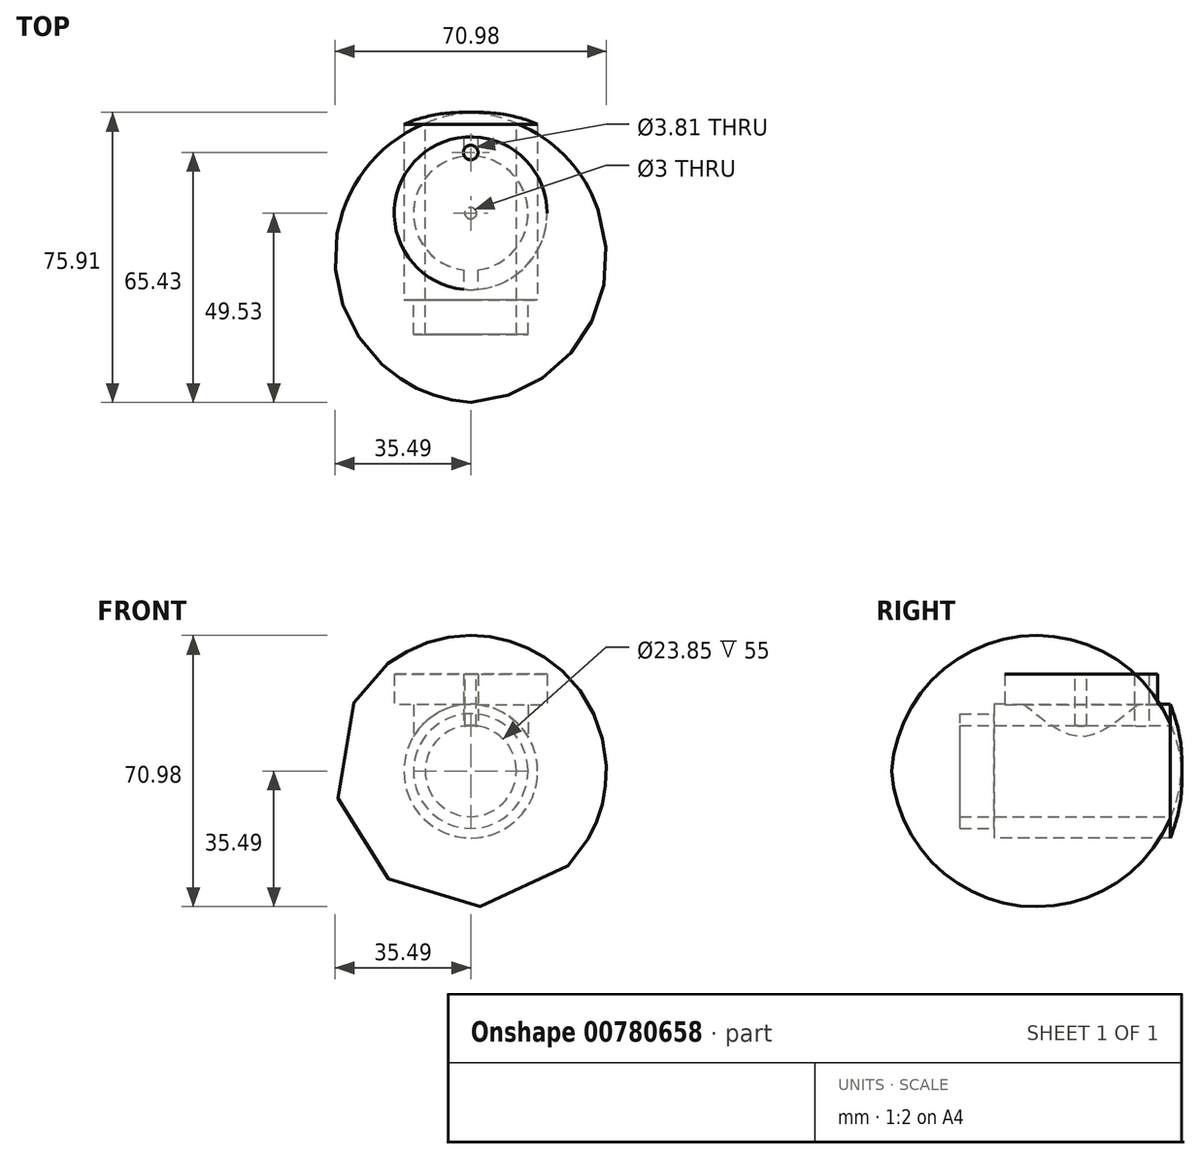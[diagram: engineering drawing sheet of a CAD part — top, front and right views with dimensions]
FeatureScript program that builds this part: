
annotation { "Feature Type Name" : "Feature", "Feature Type Description" : "" }
export const myFeature = defineFeature(function(context is Context, id is Id, definition is map)
    precondition{}
    {
        {
            var Q0;
            Q0=qCreatedBy(makeId("Front.planeOp"),FACE);
            var sketch = newSketch(context, id + "F0", { "sketchPlane" : qUnion([Q0])});
            skCircle(sketch, "E0", {"center": v(0, 0) * mm, "radius": 11.93 * mm});
            skCircle(sketch, "E1", {"center": v(0, 0) * mm, "radius": 15 * mm});
            skSolve(sketch);
        }
        {
            var Q0;
            Q0 = qSketchRegion(id + "F0", true);
            extrude(context, id + "F1", {"entities" : qUnion([Q0]), "depth" : 9 * mm, "offsetDistance" : 25 * mm});
        }
        {
            var Q0;
            Q0=makeQuery(id+"F1.opExtrude","CAP_FACE",FACE,{"disambiguationData":[OSD([sQuery(id+"F0.wireOp",EDGE,"E0"),sQuery(id+"F0.wireOp",EDGE,"E1")])],"isStart":true});
            var sketch = newSketch(context, id + "F2", { "sketchPlane" : qUnion([Q0])});
            skCircle(sketch, "E2", {"center": v(0, 0) * mm, "radius": 11.93 * mm});
            skCircle(sketch, "E3", {"center": v(0, 0) * mm, "radius": 17.5 * mm});
            skSolve(sketch);
        }
        {
            var Q0;
            Q0 = qSketchRegion(id + "F2", true);
            extrude(context, id + "F3", {"entities" : qUnion([Q0]), "operationType" : NewBodyOperationType.ADD, "depth" : 46 * mm, "offsetDistance" : 25 * mm});
        }
        {
            var Q0;
            Q0=qCreatedBy(makeId("Top.planeOp"),FACE);
            var sketch = newSketch(context, id + "F4", { "sketchPlane" : qUnion([Q0])});
            skLineSegment(sketch, "E4", {"start": v(0, 0) * mm, "end": v(0, 46) * mm});
            skLineSegment(sketch, "E5", {"start": v(0, 46) * mm, "end": v(0, 49) * mm});
            skLineSegment(sketch, "E6", {"start": v(0, 46) * mm, "end": v(-17.5, 46) * mm});
            skArc(sketch, "E7", {"start": v(0, 49) * mm, "mid": v(-8.93, 48.54) * mm, "end": v(-17.5, 46) * mm});
            skSolve(sketch);
        }
        {
            var Q0;
            Q0 = qSketchRegion(id + "F4", true);
            var Q1;
            Q1=sQuery(id+"F4.wireOp",EDGE,"E5");
            revolve(context, id + "F5", {"operationType" : NewBodyOperationType.ADD, "surfaceOperationType" : NewSurfaceOperationType.NEW, "entities" : qUnion([Q0]), "axis" : qUnion([Q1]), "revolveType" : RevolveType.FULL});
        }
        {
            var Q0;
            Q0=qCreatedBy(makeId("Top.planeOp"),FACE);
            cPlane(context, id + "F6", {"entities" : qUnion([Q0]), "cplaneType" : CPlaneType.OFFSET, "offset" : 17.4 * mm, "width" : 150 * mm, "height" : 150 * mm});
        }
        {
            var Q0;
            Q0=qCreatedBy(id+"F6.planeOp",FACE);
            var sketch = newSketch(context, id + "F7", { "sketchPlane" : qUnion([Q0])});
            skLineSegment(sketch, "E8", {"start": v(0, 0) * mm, "end": v(0, 22.7) * mm});
            skCircle(sketch, "E9", {"center": v(0, 22.7) * mm, "radius": 20 * mm});
            skCircle(sketch, "E10", {"center": v(0, 22.7) * mm, "radius": 15 * mm});
            skSolve(sketch);
        }
        {
            var Q0;
            Q0=makeQuery(id+"F7.imprint","IMPRINT",FACE,{"disambiguationData":[TD([[makeQuery(id+"F7.imprint","IMPRINT",EDGE,{"derivedFrom":sQuery(id+"F7.wireOp",EDGE,"E9")}),1.0]])]});
            extrude(context, id + "F8", {"entities" : qUnion([Q0]), "operationType" : NewBodyOperationType.ADD, "depth" : 8 * mm, "offsetDistance" : 25 * mm});
        }
        {
            var Q0;
            Q0=makeQuery(id+"F7.imprint","IMPRINT",FACE,{"disambiguationData":[TD([[makeQuery(id+"F7.imprint","IMPRINT",EDGE,{"derivedFrom":sQuery(id+"F7.wireOp",EDGE,"E10")}),1.0]])]});
            extrude(context, id + "F9", {"entities" : qUnion([Q0]), "operationType" : NewBodyOperationType.ADD, "depth" : 8 * mm, "offsetDistance" : 25 * mm, "hasSecondDirection" : true, "secondDirectionOppositeDirection" : true, "secondDirectionDepth" : 10 * mm});
        }
        {
            var Q0;
            Q0=qCreatedBy(makeId("Front.planeOp"),FACE);
            var sketch = newSketch(context, id + "F10", { "sketchPlane" : qUnion([Q0])});
            skCircle(sketch, "E11", {"center": v(0, 0) * mm, "radius": 11.93 * mm});
            skSolve(sketch);
        }
        {
            var Q0;
            Q0 = qSketchRegion(id + "F10", true);
            var Q1;
            Q1=makeQuery(id+"F5.opRevolve","SWEPT_FACE",FACE,{"disambiguationData":[OSD([sQuery(id+"F4.wireOp",EDGE,"E6")])]});
            extrude(context, id + "F11", {"entities" : qUnion([Q0]), "operationType" : NewBodyOperationType.REMOVE, "endBound" : BoundingType.UP_TO_SURFACE, "oppositeDirection" : true, "depth" : 25 * mm, "endBoundEntityFace" : qUnion([Q1]), "offsetDistance" : 25 * mm});
        }
        {
            var Q0;
            Q0=qCreatedBy(makeId("Top.planeOp"),FACE);
            var sketch = newSketch(context, id + "F12", { "sketchPlane" : qUnion([Q0])});
            skLineSegment(sketch, "E12", {"start": v(0, 0) * mm, "end": v(0, 38.6) * mm});
            skCircle(sketch, "E13", {"center": v(0, 38.6) * mm, "radius": 1.9 * mm});
            skSolve(sketch);
        }
        {
            var Q0;
            Q0 = qSketchRegion(id + "F12", true);
            extrude(context, id + "F13", {"entities" : qUnion([Q0]), "operationType" : NewBodyOperationType.REMOVE, "endBound" : BoundingType.THROUGH_ALL, "depth" : 25 * mm, "offsetDistance" : 25 * mm});
        }
        {
            var Q0;
            {var subQ0=sQuery(id+"F7.wireOp",EDGE,"E10");Q0=makeQuery(id+"F9.boolean.opBoolean","MERGE",FACE,{"derivedFrom":[makeQuery(id+"F8.opExtrude","CAP_FACE",FACE,{"disambiguationData":[OSD([sQuery(id+"F7.wireOp",EDGE,"E9"),subQ0])],"isStart":false}),makeQuery(id+"F9.opExtrude","CAP_FACE",FACE,{"disambiguationData":[OSD([subQ0])],"isStart":false})]});}
            var sketch = newSketch(context, id + "F14", { "sketchPlane" : qUnion([Q0])});
            skLineSegment(sketch, "E14", {"start": v(0, 38.6) * mm, "end": v(0, 22.7) * mm});
            skCircle(sketch, "E15", {"center": v(0, 22.7) * mm, "radius": 1.5 * mm});
            skSolve(sketch);
        }
        {
            var Q0;
            Q0 = qSketchRegion(id + "F14", true);
            extrude(context, id + "F15", {"entities" : qUnion([Q0]), "operationType" : NewBodyOperationType.REMOVE, "oppositeDirection" : true, "depth" : 25 * mm, "offsetDistance" : 25 * mm});
        }
    });
